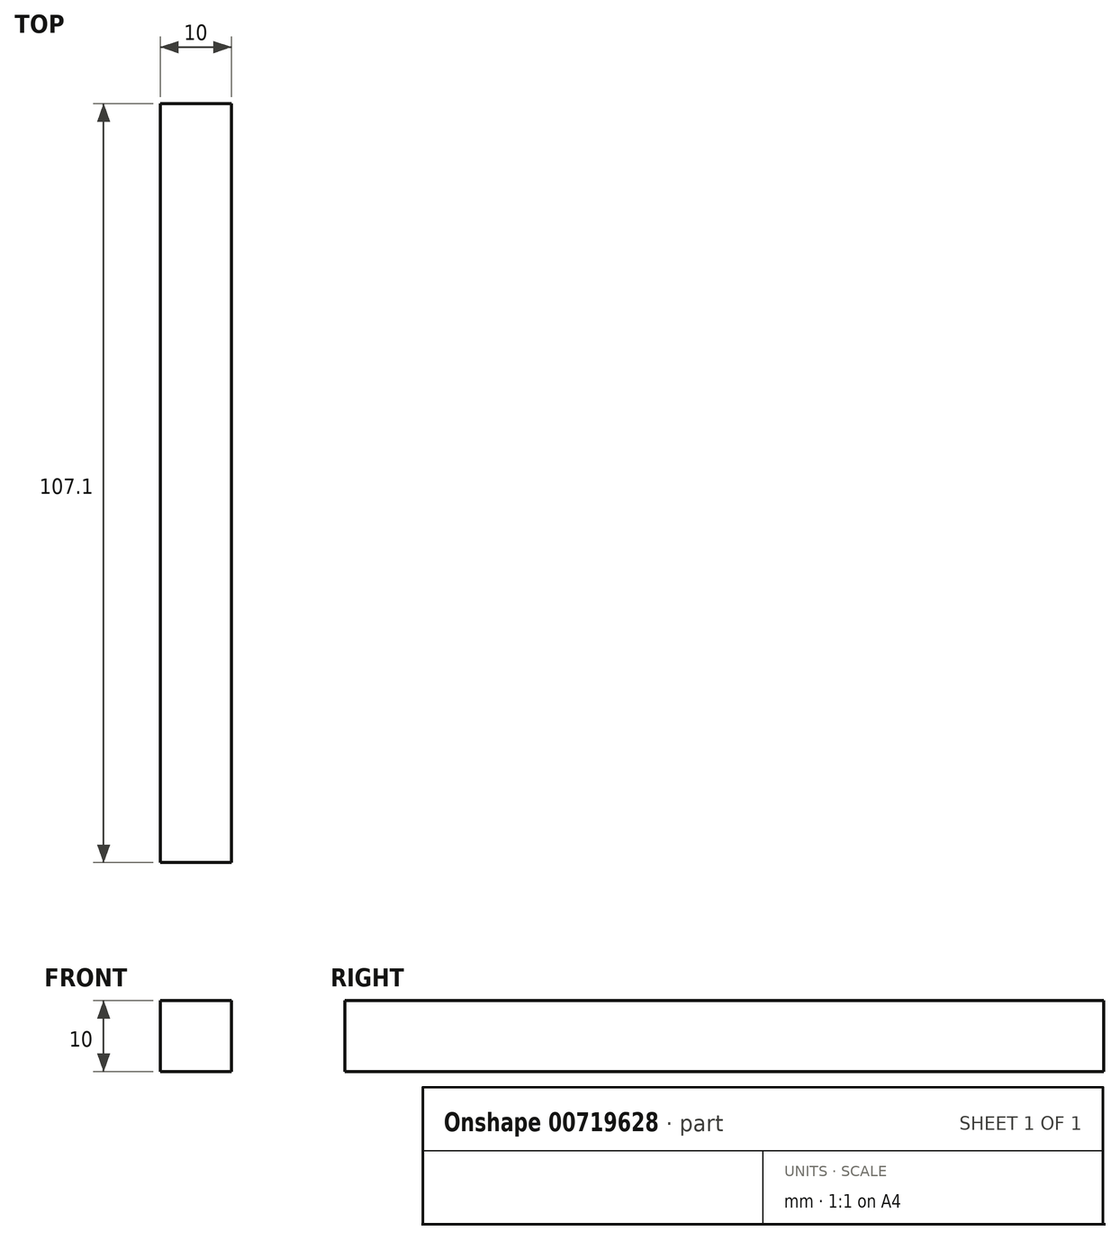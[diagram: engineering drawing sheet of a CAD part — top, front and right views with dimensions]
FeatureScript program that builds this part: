
annotation { "Feature Type Name" : "Feature", "Feature Type Description" : "" }
export const myFeature = defineFeature(function(context is Context, id is Id, definition is map)
    precondition{}
    {
        {
            var Q0;
            Q0=qCreatedBy(makeId("Front.planeOp"),FACE);
            var sketch = newSketch(context, id + "F0", { "sketchPlane" : qUnion([Q0])});
            skLineSegment(sketch, "E0.bottom", {"start": v(-65.47, 43.47) * mm, "end": v(-55.47, 43.47) * mm});
            skLineSegment(sketch, "E0.top", {"start": v(-65.47, 33.47) * mm, "end": v(-55.47, 33.47) * mm});
            skLineSegment(sketch, "E0.left", {"start": v(-65.47, 43.47) * mm, "end": v(-65.47, 33.47) * mm});
            skLineSegment(sketch, "E0.right", {"start": v(-55.47, 43.47) * mm, "end": v(-55.47, 33.47) * mm});
            skSolve(sketch);
        }
        {
            var Q0;
            Q0=makeQuery(id+"F0.imprint","IMPRINT",FACE,{"disambiguationData":[TD([[makeQuery(id+"F0.imprint","IMPRINT",EDGE,{"derivedFrom":sQuery(id+"F0.wireOp",EDGE,"E0.bottom")}),-1.0]])]});
            extrude(context, id + "F1", {"entities" : qUnion([Q0]), "depth" : 107.1 * mm});
        }
    });
